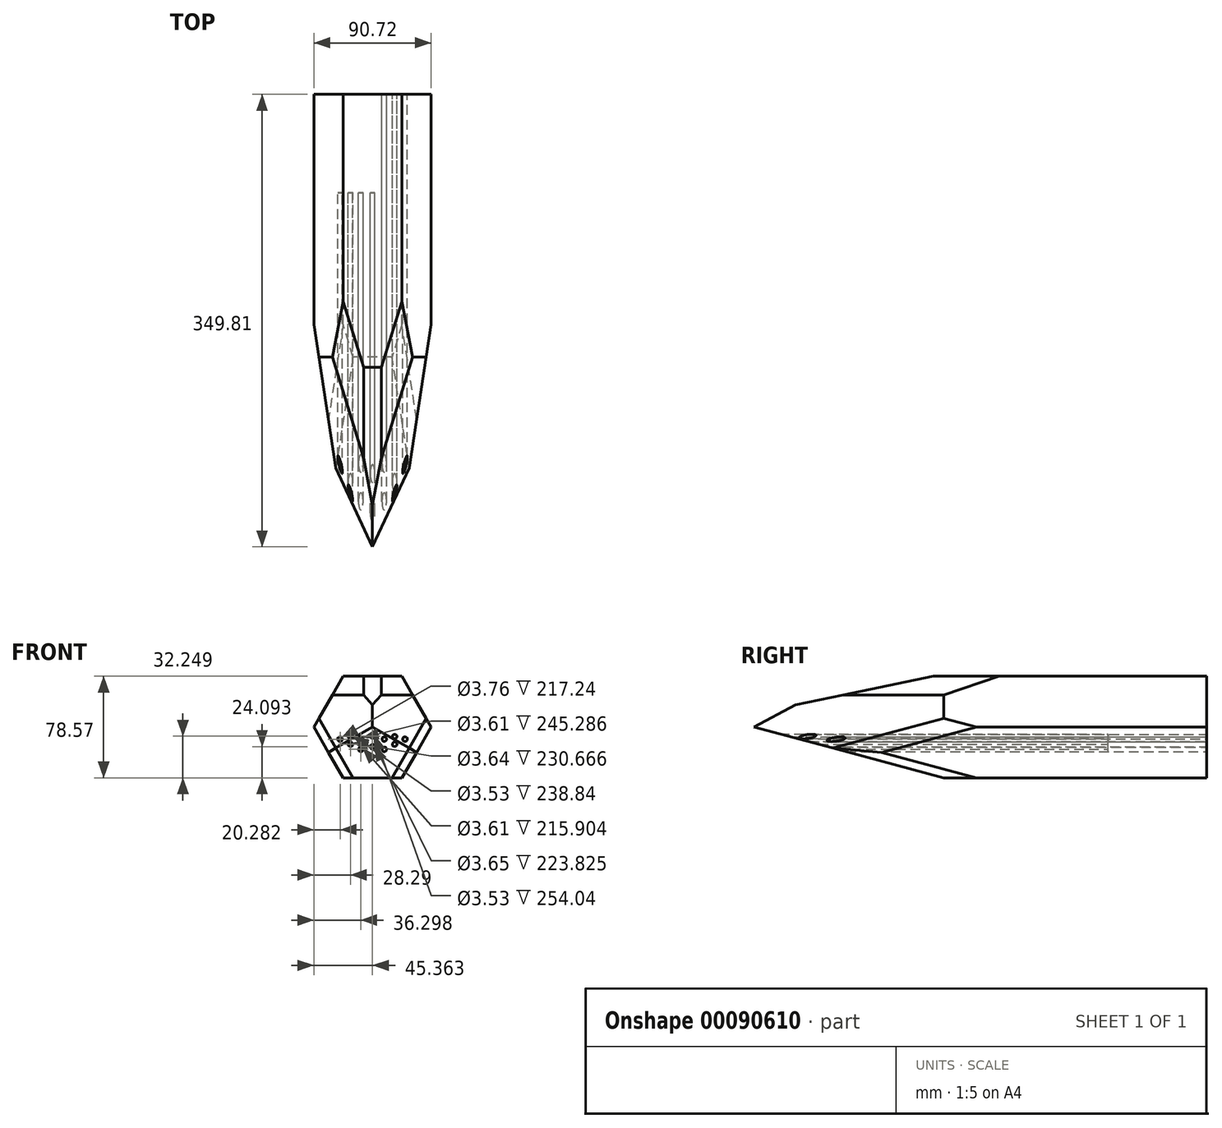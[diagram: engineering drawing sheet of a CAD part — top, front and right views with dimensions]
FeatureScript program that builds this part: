
annotation { "Feature Type Name" : "Feature", "Feature Type Description" : "" }
export const myFeature = defineFeature(function(context is Context, id is Id, definition is map)
    precondition{}
    {
        {
            var Q0;
            Q0=qCreatedBy(makeId("Front.planeOp"),FACE);
            var sketch = newSketch(context, id + "F0", { "sketchPlane" : qUnion([Q0])});
            skCircle(sketch, "E0.cCircle", {"center": v(-15.5, 39.28) * mm, "radius": 39.28 * mm, "construction": true});
            skLineSegment(sketch, "E0.0", {"start": v(7.18, 0) * mm, "end": v(-38.18, 0) * mm});
            skLineSegment(sketch, "E0.1", {"start": v(-38.18, 0) * mm, "end": v(-60.86, 39.28) * mm});
            skLineSegment(sketch, "E0.2", {"start": v(-60.86, 39.28) * mm, "end": v(-38.18, 78.57) * mm});
            skLineSegment(sketch, "E0.3", {"start": v(-38.18, 78.57) * mm, "end": v(7.18, 78.57) * mm});
            skLineSegment(sketch, "E0.4", {"start": v(7.18, 78.57) * mm, "end": v(29.86, 39.28) * mm});
            skLineSegment(sketch, "E0.5", {"start": v(29.86, 39.28) * mm, "end": v(7.18, 0) * mm});
            skPoint(sketch, "E0.0.midPoint", {"position": v(-15.5, 0) * mm});
            skLineSegment(sketch, "E1", {"start": v(-15.5, 78.57) * mm, "end": v(-15.5, 155.68) * mm});
            skLineSegment(sketch, "E2", {"start": v(-15.5, 39.28) * mm, "end": v(-15.5, 78.57) * mm});
            skCircle(sketch, "E3", {"center": v(-40.58, 29.87) * mm, "radius": 1.88 * mm});
            skCircle(sketch, "E4", {"center": v(-24.56, 22) * mm, "radius": 1.8 * mm});
            skLineSegment(sketch, "E5", {"start": v(-24.56, 22) * mm, "end": v(-24.56, 35.15) * mm});
            skCircle(sketch, "E6", {"center": v(-24.56, 29.87) * mm, "radius": 1.8 * mm});
            skPoint(sketch, "E6.centerSnap0", {"position": v(-24.56, 28.57) * mm});
            skLineSegment(sketch, "E7", {"start": v(-40.58, 29.87) * mm, "end": v(-24.56, 22) * mm});
            skCircle(sketch, "E8", {"center": v(-32.57, 25.93) * mm, "radius": 1.82 * mm});
            skLineSegment(sketch, "E9", {"start": v(-32.57, 25.93) * mm, "end": v(-32.57, 31.93) * mm});
            skCircle(sketch, "E10", {"center": v(-32.57, 31.93) * mm, "radius": 1.77 * mm});
            skCircle(sketch, "E11.MirrorC", {"center": v(-6.43, 29.87) * mm, "radius": 1.8 * mm});
            skCircle(sketch, "E12.MirrorC", {"center": v(-6.43, 22) * mm, "radius": 1.8 * mm});
            skCircle(sketch, "E13.MirrorC", {"center": v(1.58, 25.93) * mm, "radius": 1.82 * mm});
            skCircle(sketch, "E14.MirrorC", {"center": v(1.58, 31.93) * mm, "radius": 1.77 * mm});
            skCircle(sketch, "E15.MirrorC", {"center": v(9.58, 29.87) * mm, "radius": 1.88 * mm});
            skCircle(sketch, "E16", {"center": v(-15.5, 32.25) * mm, "radius": 1.77 * mm});
            skCircle(sketch, "E17", {"center": v(-15.5, 24.1) * mm, "radius": 1.83 * mm});
            skSolve(sketch);
        }
        {
            var Q0;
            Q0=makeQuery(id+"F0.imprint","IMPRINT",FACE,{"disambiguationData":[TD([[makeQuery(id+"F0.imprint","IMPRINT",EDGE,{"derivedFrom":sQuery(id+"F0.wireOp",EDGE,"E0.0")}),-1.0]])]});
            extrude(context, id + "F1", {"entities" : qUnion([Q0]), "depth" : 355.6 * mm});
        }
        {
            var Q0;
            Q0=makeQuery(id+"F1.opExtrude","CAP_EDGE",EDGE,{"disambiguationData":[OSD([sQuery(id+"F0.wireOp",EDGE,"E0.4")])],"isStart":false});
            var Q1;
            Q1=makeQuery(id+"F1.opExtrude","CAP_EDGE",EDGE,{"disambiguationData":[OSD([sQuery(id+"F0.wireOp",EDGE,"E0.0")])],"isStart":false});
            var Q2;
            Q2=makeQuery(id+"F1.opExtrude","CAP_EDGE",EDGE,{"disambiguationData":[OSD([sQuery(id+"F0.wireOp",EDGE,"E0.2")])],"isStart":false});
            chamfer(context, id + "F2", {"entities" : qUnion([Q0, Q1, Q2]), "chamferType" : ChamferType.OFFSET_ANGLE, "width" : 152.4 * mm, "oppositeDirection" : false, "angle" : 15 * degree, "tangentPropagation" : true});
        }
        {
            var Q0;
            Q0=makeQuery(id+"F2.opChamfer","BLEND_EDGE",EDGE,{"blendedFrom":[makeQuery(id+"F1.opExtrude","CAP_EDGE",EDGE,{"disambiguationData":[OSD([sQuery(id+"F0.wireOp",EDGE,"E0.4")])],"isStart":false}),makeQuery(id+"F1.opExtrude","SWEPT_FACE",FACE,{"disambiguationData":[OSD([sQuery(id+"F0.wireOp",EDGE,"E0.3")])]})],"blendedInto":[makeQuery(id+"F1.opExtrude","SWEPT_FACE",FACE,{"disambiguationData":[OSD([sQuery(id+"F0.wireOp",EDGE,"E0.3")])]})]});
            var Q1;
            Q1=makeQuery(id+"F2.opChamfer","BLEND_EDGE",EDGE,{"blendedFrom":[makeQuery(id+"F1.opExtrude","CAP_EDGE",EDGE,{"disambiguationData":[OSD([sQuery(id+"F0.wireOp",EDGE,"E0.2")])],"isStart":false}),makeQuery(id+"F1.opExtrude","SWEPT_FACE",FACE,{"disambiguationData":[OSD([sQuery(id+"F0.wireOp",EDGE,"E0.3")])]})],"blendedInto":[makeQuery(id+"F1.opExtrude","SWEPT_FACE",FACE,{"disambiguationData":[OSD([sQuery(id+"F0.wireOp",EDGE,"E0.3")])]})]});
            chamfer(context, id + "F3", {"entities" : qUnion([Q0, Q1]), "chamferType" : ChamferType.OFFSET_ANGLE, "width" : 12.7 * mm, "oppositeDirection" : false, "angle" : 35 * degree, "tangentPropagation" : true});
        }
        {
            var Q0;
            {var subQ0=makeQuery(id+"F1.opExtrude","SWEPT_FACE",FACE,{"disambiguationData":[OSD([sQuery(id+"F0.wireOp",EDGE,"E0.3")])]});Q0=makeQuery(id+"F3.opChamfer","BLEND_EDGE",EDGE,{"blendedFrom":[makeQuery(id+"F2.opChamfer","BLEND_EDGE",EDGE,{"blendedFrom":[makeQuery(id+"F1.opExtrude","CAP_EDGE",EDGE,{"disambiguationData":[OSD([sQuery(id+"F0.wireOp",EDGE,"E0.2")])],"isStart":false}),subQ0],"blendedInto":[subQ0]}),makeQuery(id+"F2.opChamfer","BLEND_EDGE",EDGE,{"blendedFrom":[makeQuery(id+"F1.opExtrude","CAP_EDGE",EDGE,{"disambiguationData":[OSD([sQuery(id+"F0.wireOp",EDGE,"E0.4")])],"isStart":false}),subQ0],"blendedInto":[subQ0]})],"blendedInto":[]});}
            chamfer(context, id + "F4", {"entities" : qUnion([Q0]), "width" : 12.7 * mm, "tangentPropagation" : true});
        }
        {
            var Q0;
            Q0=makeQuery(id+"F2.opChamfer","BLEND_EDGE",EDGE,{"blendedFrom":[makeQuery(id+"F1.opExtrude","CAP_EDGE",EDGE,{"disambiguationData":[OSD([sQuery(id+"F0.wireOp",EDGE,"E0.0")])],"isStart":false}),makeQuery(id+"F1.opExtrude","SWEPT_FACE",FACE,{"disambiguationData":[OSD([sQuery(id+"F0.wireOp",EDGE,"E0.1")])]})],"blendedInto":[makeQuery(id+"F1.opExtrude","SWEPT_FACE",FACE,{"disambiguationData":[OSD([sQuery(id+"F0.wireOp",EDGE,"E0.1")])]})]});
            var Q1;
            Q1=makeQuery(id+"F2.opChamfer","BLEND_EDGE",EDGE,{"blendedFrom":[makeQuery(id+"F1.opExtrude","CAP_EDGE",EDGE,{"disambiguationData":[OSD([sQuery(id+"F0.wireOp",EDGE,"E0.0")])],"isStart":false}),makeQuery(id+"F1.opExtrude","SWEPT_FACE",FACE,{"disambiguationData":[OSD([sQuery(id+"F0.wireOp",EDGE,"E0.5")])]})],"blendedInto":[makeQuery(id+"F1.opExtrude","SWEPT_FACE",FACE,{"disambiguationData":[OSD([sQuery(id+"F0.wireOp",EDGE,"E0.5")])]})]});
            var Q2;
            Q2=makeQuery(id+"F2.opChamfer","BLEND_EDGE",EDGE,{"blendedFrom":[makeQuery(id+"F1.opExtrude","CAP_EDGE",EDGE,{"disambiguationData":[OSD([sQuery(id+"F0.wireOp",EDGE,"E0.4")])],"isStart":false}),makeQuery(id+"F1.opExtrude","SWEPT_FACE",FACE,{"disambiguationData":[OSD([sQuery(id+"F0.wireOp",EDGE,"E0.5")])]})],"blendedInto":[makeQuery(id+"F1.opExtrude","SWEPT_FACE",FACE,{"disambiguationData":[OSD([sQuery(id+"F0.wireOp",EDGE,"E0.5")])]})]});
            var Q3;
            Q3=makeQuery(id+"F2.opChamfer","BLEND_EDGE",EDGE,{"blendedFrom":[makeQuery(id+"F1.opExtrude","CAP_EDGE",EDGE,{"disambiguationData":[OSD([sQuery(id+"F0.wireOp",EDGE,"E0.2")])],"isStart":false}),makeQuery(id+"F1.opExtrude","SWEPT_FACE",FACE,{"disambiguationData":[OSD([sQuery(id+"F0.wireOp",EDGE,"E0.1")])]})],"blendedInto":[makeQuery(id+"F1.opExtrude","SWEPT_FACE",FACE,{"disambiguationData":[OSD([sQuery(id+"F0.wireOp",EDGE,"E0.1")])]})]});
            chamfer(context, id + "F5", {"entities" : qUnion([Q0, Q1, Q2, Q3]), "width" : 12.7 * mm, "tangentPropagation" : true});
        }
        {
            var Q0;
            Q0=makeQuery(id+"F1.opExtrude","SWEPT_FACE",FACE,{"disambiguationData":[OSD([sQuery(id+"F0.wireOp",EDGE,"E0.3")])]});
            var sketch = newSketch(context, id + "F6", { "sketchPlane" : qUnion([Q0])});
            skArc(sketch, "E18", {"start": v(-15.5, 0) * mm, "mid": v(-17.4, -33.66) * mm, "end": v(-15.5, -67.31) * mm});
            skArc(sketch, "E19.MirrorCS", {"start": v(-15.5, 0) * mm, "mid": v(-13.59, -33.66) * mm, "end": v(-15.5, -67.31) * mm});
            skLineSegment(sketch, "E20", {"start": v(-15.5, -67.31) * mm, "end": v(-15.5, 0) * mm});
            skCircle(sketch, "E21", {"center": v(-15.5, -33.66) * mm, "radius": 2.22 * mm});
            skSolve(sketch);
        }
        {
            var Q0;
            Q0=makeQuery(id+"F0.imprint","IMPRINT",FACE,{"disambiguationData":[TD([[makeQuery(id+"F0.imprint","IMPRINT",EDGE,{"derivedFrom":sQuery(id+"F0.wireOp",EDGE,"E0.0")}),-1.0]])]});
            var sketch = newSketch(context, id + "F7", { "sketchPlane" : qUnion([Q0])});
            skSolve(sketch);
        }
        {
            var Q0;
            Q0=makeQuery(id+"F7.imprint","IMPRINT",FACE,{"disambiguationData":[TD([[makeQuery(id+"F7.imprint","IMPRINT",EDGE,{"derivedFrom":makeQuery(id+"F0.imprint","IMPRINT",EDGE,{"derivedFrom":sQuery(id+"F0.wireOp",EDGE,"E0.0")})}),-1.0]])]});
            var sketch = newSketch(context, id + "F8", { "sketchPlane" : qUnion([Q0])});
            skCircle(sketch, "E22", {"center": v(0, 38.74) * mm, "radius": 12.67 * mm});
            skCircle(sketch, "E23.MirrorC", {"center": v(-30.94, 38.75) * mm, "radius": 12.67 * mm});
            skCircle(sketch, "E24", {"center": v(-15.47, 56.6) * mm, "radius": 8.66 * mm});
            skCircle(sketch, "E25.MirrorC", {"center": v(-15.48, 20.89) * mm, "radius": 8.66 * mm});
            skCircle(sketch, "E26", {"center": v(-30.73, 57.58) * mm, "radius": 3.79 * mm});
            skCircle(sketch, "E27.MirrorC", {"center": v(-0.2, 57.57) * mm, "radius": 3.79 * mm});
            skCircle(sketch, "E28.MirrorC", {"center": v(-30.74, 19.92) * mm, "radius": 3.79 * mm});
            skCircle(sketch, "E29.MirrorC", {"center": v(-0.22, 19.91) * mm, "radius": 3.79 * mm});
            skSolve(sketch);
        }
        {
            var Q0;
            Q0=sQuery(id+"F8.wireOp",VERTEX,"E24.center");
            var Q1;
            Q1=sQuery(id+"F8.wireOp",VERTEX,"E25.MirrorC.center");
            var Q2;
            Q2=makeQuery(id+"F1.opExtrude","SWEPT_BODY",BODY,{"disambiguationData":[OSD([sQuery(id+"F0.wireOp",EDGE,"E0.0"),sQuery(id+"F0.wireOp",EDGE,"E0.1"),sQuery(id+"F0.wireOp",EDGE,"E0.2"),sQuery(id+"F0.wireOp",EDGE,"E0.3"),sQuery(id+"F0.wireOp",EDGE,"E0.4"),sQuery(id+"F0.wireOp",EDGE,"E0.5")])]});
            hole(context, id + "F9", {"style" : HoleStyle.SIMPLE, "endStyle" : HoleEndStyle.BLIND, "oppositeDirection" : true, "holeDiameter" : 17.78 * mm, "holeDepth" : 12.7 * mm, "locations" : qUnion([Q0, Q1]), "scope" : qUnion([Q2])});
        }
        {
            var Q0;
            Q0=sQuery(id+"F8.wireOp",VERTEX,"E26.center");
            var Q1;
            Q1=sQuery(id+"F8.wireOp",VERTEX,"E28.MirrorC.center");
            var Q2;
            Q2=sQuery(id+"F8.wireOp",VERTEX,"E29.MirrorC.center");
            var Q3;
            Q3=sQuery(id+"F8.wireOp",VERTEX,"E27.MirrorC.center");
            var Q4;
            Q4=makeQuery(id+"F1.opExtrude","SWEPT_BODY",BODY,{"disambiguationData":[OSD([sQuery(id+"F0.wireOp",EDGE,"E0.0"),sQuery(id+"F0.wireOp",EDGE,"E0.1"),sQuery(id+"F0.wireOp",EDGE,"E0.2"),sQuery(id+"F0.wireOp",EDGE,"E0.3"),sQuery(id+"F0.wireOp",EDGE,"E0.4"),sQuery(id+"F0.wireOp",EDGE,"E0.5")])]});
            hole(context, id + "F10", {"style" : HoleStyle.SIMPLE, "endStyle" : HoleEndStyle.BLIND, "oppositeDirection" : true, "holeDiameter" : 7.62 * mm, "holeDepth" : 12.7 * mm, "locations" : qUnion([Q0, Q1, Q2, Q3]), "scope" : qUnion([Q4])});
        }
        {
            var Q0;
            Q0=sQuery(id+"F8.wireOp",VERTEX,"E22.center");
            var Q1;
            Q1=sQuery(id+"F8.wireOp",VERTEX,"E23.MirrorC.center");
            var Q2;
            Q2=makeQuery(id+"F1.opExtrude","SWEPT_BODY",BODY,{"disambiguationData":[OSD([sQuery(id+"F0.wireOp",EDGE,"E0.0"),sQuery(id+"F0.wireOp",EDGE,"E0.1"),sQuery(id+"F0.wireOp",EDGE,"E0.2"),sQuery(id+"F0.wireOp",EDGE,"E0.3"),sQuery(id+"F0.wireOp",EDGE,"E0.4"),sQuery(id+"F0.wireOp",EDGE,"E0.5")])]});
            hole(context, id + "F11", {"style" : HoleStyle.SIMPLE, "endStyle" : HoleEndStyle.BLIND, "oppositeDirection" : true, "holeDiameter" : 25.4 * mm, "holeDepth" : 12.7 * mm, "locations" : qUnion([Q0, Q1]), "scope" : qUnion([Q2])});
        }
        {
            var Q0;
            Q0=sQuery(id+"F6.wireOp",VERTEX,"E21.center");
            var Q1;
            Q1=makeQuery(id+"F1.opExtrude","SWEPT_BODY",BODY,{"disambiguationData":[OSD([sQuery(id+"F0.wireOp",EDGE,"E0.0"),sQuery(id+"F0.wireOp",EDGE,"E0.1"),sQuery(id+"F0.wireOp",EDGE,"E0.2"),sQuery(id+"F0.wireOp",EDGE,"E0.3"),sQuery(id+"F0.wireOp",EDGE,"E0.4"),sQuery(id+"F0.wireOp",EDGE,"E0.5")])]});
            hole(context, id + "F12", {"style" : HoleStyle.SIMPLE, "endStyle" : HoleEndStyle.BLIND, "holeDiameter" : 4.44 * mm, "holeDepth" : 6.35 * mm, "locations" : qUnion([Q0]), "scope" : qUnion([Q1])});
        }
        {
            var Q0;
            Q0=makeQuery(id+"F1.opExtrude","SWEPT_FACE",FACE,{"disambiguationData":[OSD([sQuery(id+"F0.wireOp",EDGE,"E0.5")])]});
            var sketch = newSketch(context, id + "F13", { "sketchPlane" : qUnion([Q0])});
            skLineSegment(sketch, "E30", {"start": v(0, 26.27) * mm, "end": v(-33.66, 26.27) * mm});
            skSolve(sketch);
        }
        {
            var Q0;
            Q0=sQuery(id+"F13.wireOp",VERTEX,"E30.end");
            var Q1;
            Q1=makeQuery(id+"F1.opExtrude","SWEPT_BODY",BODY,{"disambiguationData":[OSD([sQuery(id+"F0.wireOp",EDGE,"E0.0"),sQuery(id+"F0.wireOp",EDGE,"E0.1"),sQuery(id+"F0.wireOp",EDGE,"E0.2"),sQuery(id+"F0.wireOp",EDGE,"E0.3"),sQuery(id+"F0.wireOp",EDGE,"E0.4"),sQuery(id+"F0.wireOp",EDGE,"E0.5")])]});
            hole(context, id + "F14", {"style" : HoleStyle.SIMPLE, "endStyle" : HoleEndStyle.BLIND, "holeDiameter" : 4.44 * mm, "holeDepth" : 6.35 * mm, "locations" : qUnion([Q0]), "scope" : qUnion([Q1])});
        }
        {
            var Q0;
            Q0=makeQuery(id+"F1.opExtrude","SWEPT_FACE",FACE,{"disambiguationData":[OSD([sQuery(id+"F0.wireOp",EDGE,"E0.1")])]});
            var sketch = newSketch(context, id + "F15", { "sketchPlane" : qUnion([Q0])});
            skLineSegment(sketch, "E31", {"start": v(0, 41.77) * mm, "end": v(33.66, 41.77) * mm});
            skSolve(sketch);
        }
        {
            var Q0;
            Q0=sQuery(id+"F15.wireOp",VERTEX,"E31.end");
            var Q1;
            Q1=makeQuery(id+"F1.opExtrude","SWEPT_BODY",BODY,{"disambiguationData":[OSD([sQuery(id+"F0.wireOp",EDGE,"E0.0"),sQuery(id+"F0.wireOp",EDGE,"E0.1"),sQuery(id+"F0.wireOp",EDGE,"E0.2"),sQuery(id+"F0.wireOp",EDGE,"E0.3"),sQuery(id+"F0.wireOp",EDGE,"E0.4"),sQuery(id+"F0.wireOp",EDGE,"E0.5")])]});
            hole(context, id + "F16", {"style" : HoleStyle.SIMPLE, "endStyle" : HoleEndStyle.BLIND, "holeDiameter" : 4.44 * mm, "holeDepth" : 6.35 * mm, "locations" : qUnion([Q0]), "scope" : qUnion([Q1])});
        }
        {
            var Q0;
            Q0=makeQuery(id+"F0.imprint","IMPRINT",FACE,{"disambiguationData":[TD([[makeQuery(id+"F0.imprint","IMPRINT",EDGE,{"derivedFrom":sQuery(id+"F0.wireOp",EDGE,"E3")}),1.0]])]});
            var Q1;
            {var subQ0=sQuery(id+"F0.wireOp",EDGE,"E7");var subQ1=makeQuery(id+"F0.imprint","INTERSECT",VERTEX,{"derivedFrom":[subQ0,sQuery(id+"F0.wireOp",EDGE,"E9")]});Q1=makeQuery(id+"F0.imprint","IMPRINT",FACE,{"disambiguationData":[TD([[makeQuery(id+"F0.imprint","IMPRINT",EDGE,{"disambiguationData":[TD([[subQ1,1.0]])],"derivedFrom":subQ0}),-1.0]])]});}
            var Q2;
            {var subQ0=sQuery(id+"F0.wireOp",EDGE,"E9");var subQ1=sQuery(id+"F0.wireOp",EDGE,"E7");var subQ2=makeQuery(id+"F0.imprint","INTERSECT",VERTEX,{"derivedFrom":[subQ1,subQ0]});Q2=makeQuery(id+"F0.imprint","IMPRINT",FACE,{"disambiguationData":[TD([[makeQuery(id+"F0.imprint","IMPRINT",EDGE,{"disambiguationData":[TD([[subQ2,-1.0]])],"derivedFrom":subQ1}),1.0]])]});}
            var Q3;
            {var subQ0=sQuery(id+"F0.wireOp",EDGE,"E9");var subQ1=sQuery(id+"F0.wireOp",EDGE,"E7");var subQ2=makeQuery(id+"F0.imprint","INTERSECT",VERTEX,{"derivedFrom":[subQ1,subQ0]});Q3=makeQuery(id+"F0.imprint","IMPRINT",FACE,{"disambiguationData":[TD([[makeQuery(id+"F0.imprint","IMPRINT",EDGE,{"disambiguationData":[TD([[subQ2,1.0]])],"derivedFrom":subQ1}),1.0]])]});}
            var Q4;
            Q4=makeQuery(id+"F0.imprint","IMPRINT",FACE,{"disambiguationData":[TD([[makeQuery(id+"F0.imprint","IMPRINT",EDGE,{"derivedFrom":sQuery(id+"F0.wireOp",EDGE,"E10")}),1.0]])]});
            var Q5;
            {var subQ0=sQuery(id+"F0.wireOp",EDGE,"E6");var subQ1=sQuery(id+"F0.wireOp",EDGE,"E5");var subQ2=makeQuery(id+"F0.imprint","INTERSECT",VERTEX,{"disambiguationData":[OD(0.0)],"derivedFrom":[subQ1,subQ0]});Q5=makeQuery(id+"F0.imprint","IMPRINT",FACE,{"disambiguationData":[TD([[makeQuery(id+"F0.imprint","IMPRINT",EDGE,{"disambiguationData":[TD([[subQ2,-1.0]])],"derivedFrom":subQ1}),1.0]])]});}
            var Q6;
            {var subQ0=sQuery(id+"F0.wireOp",EDGE,"E6");var subQ1=sQuery(id+"F0.wireOp",EDGE,"E5");var subQ2=makeQuery(id+"F0.imprint","INTERSECT",VERTEX,{"disambiguationData":[OD(0.0)],"derivedFrom":[subQ1,subQ0]});Q6=makeQuery(id+"F0.imprint","IMPRINT",FACE,{"disambiguationData":[TD([[makeQuery(id+"F0.imprint","IMPRINT",EDGE,{"disambiguationData":[TD([[subQ2,-1.0]])],"derivedFrom":subQ1}),-1.0]])]});}
            var Q7;
            {var subQ0=sQuery(id+"F0.wireOp",EDGE,"E5");var subQ1=sQuery(id+"F0.wireOp",EDGE,"E4");var subQ2=makeQuery(id+"F0.imprint","INTERSECT",VERTEX,{"derivedFrom":[subQ1,subQ0]});Q7=makeQuery(id+"F0.imprint","IMPRINT",FACE,{"disambiguationData":[TD([[makeQuery(id+"F0.imprint","IMPRINT",EDGE,{"disambiguationData":[TD([[subQ2,1.0]])],"derivedFrom":subQ1}),1.0]])]});}
            var Q8;
            {var subQ0=sQuery(id+"F0.wireOp",EDGE,"E5");var subQ1=sQuery(id+"F0.wireOp",EDGE,"E4");var subQ2=makeQuery(id+"F0.imprint","INTERSECT",VERTEX,{"derivedFrom":[subQ1,subQ0]});Q8=makeQuery(id+"F0.imprint","IMPRINT",FACE,{"disambiguationData":[TD([[makeQuery(id+"F0.imprint","IMPRINT",EDGE,{"disambiguationData":[TD([[subQ2,-1.0]])],"derivedFrom":subQ1}),1.0]])]});}
            var Q9;
            Q9=makeQuery(id+"F0.imprint","IMPRINT",FACE,{"disambiguationData":[TD([[makeQuery(id+"F0.imprint","IMPRINT",EDGE,{"derivedFrom":sQuery(id+"F0.wireOp",EDGE,"E17")}),1.0]])]});
            var Q10;
            Q10=makeQuery(id+"F0.imprint","IMPRINT",FACE,{"disambiguationData":[TD([[makeQuery(id+"F0.imprint","IMPRINT",EDGE,{"derivedFrom":sQuery(id+"F0.wireOp",EDGE,"E16")}),1.0]])]});
            var Q11;
            Q11=makeQuery(id+"F0.imprint","IMPRINT",FACE,{"disambiguationData":[TD([[makeQuery(id+"F0.imprint","IMPRINT",EDGE,{"derivedFrom":sQuery(id+"F0.wireOp",EDGE,"E11.MirrorC")}),-1.0]])]});
            var Q12;
            Q12=makeQuery(id+"F0.imprint","IMPRINT",FACE,{"disambiguationData":[TD([[makeQuery(id+"F0.imprint","IMPRINT",EDGE,{"derivedFrom":sQuery(id+"F0.wireOp",EDGE,"E12.MirrorC")}),-1.0]])]});
            var Q13;
            Q13=makeQuery(id+"F0.imprint","IMPRINT",FACE,{"disambiguationData":[TD([[makeQuery(id+"F0.imprint","IMPRINT",EDGE,{"derivedFrom":sQuery(id+"F0.wireOp",EDGE,"E13.MirrorC")}),-1.0]])]});
            var Q14;
            Q14=makeQuery(id+"F0.imprint","IMPRINT",FACE,{"disambiguationData":[TD([[makeQuery(id+"F0.imprint","IMPRINT",EDGE,{"derivedFrom":sQuery(id+"F0.wireOp",EDGE,"E14.MirrorC")}),-1.0]])]});
            var Q15;
            Q15=makeQuery(id+"F0.imprint","IMPRINT",FACE,{"disambiguationData":[TD([[makeQuery(id+"F0.imprint","IMPRINT",EDGE,{"derivedFrom":sQuery(id+"F0.wireOp",EDGE,"E15.MirrorC")}),-1.0]])]});
            extrude(context, id + "F17", {"entities" : qUnion([Q0, Q1, Q2, Q3, Q4, Q5, Q6, Q7, Q8, Q9, Q10, Q11, Q12, Q13, Q14, Q15]), "operationType" : NewBodyOperationType.ADD, "depth" : 76.2 * mm});
        }
    });
